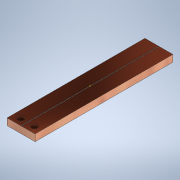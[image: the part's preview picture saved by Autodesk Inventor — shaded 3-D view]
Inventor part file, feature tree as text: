
AUTODESK INVENTOR PART (.ipt)
format: ipt  version: 2021 (Build 250183000, 183)  size: 155,648 bytes
history: native  units: in
note: dims shown in document units (in); Inventor stores cm internally (conversion verified against a paired STEP export)
features: projected_geometry x5, sketch x4, extrude x3
ambient origin geometry x8: Origin, YZ Plane, XZ Plane, XY Plane, X Axis, Y Axis, Z Axis, Center Point
bodies: Solid1 (feature_tree)
feature tree (12):
  extrude  "Extrusion1"  Depth=1.0in
  extrude  "Extrusion2"  Depth=0.047in
  sketch  "Sketch3"  dims[d5=0.047in d8=0.05in]
  extrude  "Extrusion3"  Depth=0.047in
  sketch  "Sketch1"  dims[d0=0.203in d1=1.0in]
  sketch  "Sketch2"  dims[d2=0.047in d3=0.0in d4=0.047in]
  projected_geometry  "Projected Loop1"
  sketch  "Sketch4"  dims[d9=0.004in d10=0.0015in d11=0.0in d12=0.0in d13=0.0in]
  projected_geometry  "Projected Loop2"
  projected_geometry  "Projected Loop3"
  projected_geometry  "Projected Loop4"
  projected_geometry  "Projected Loop5"
